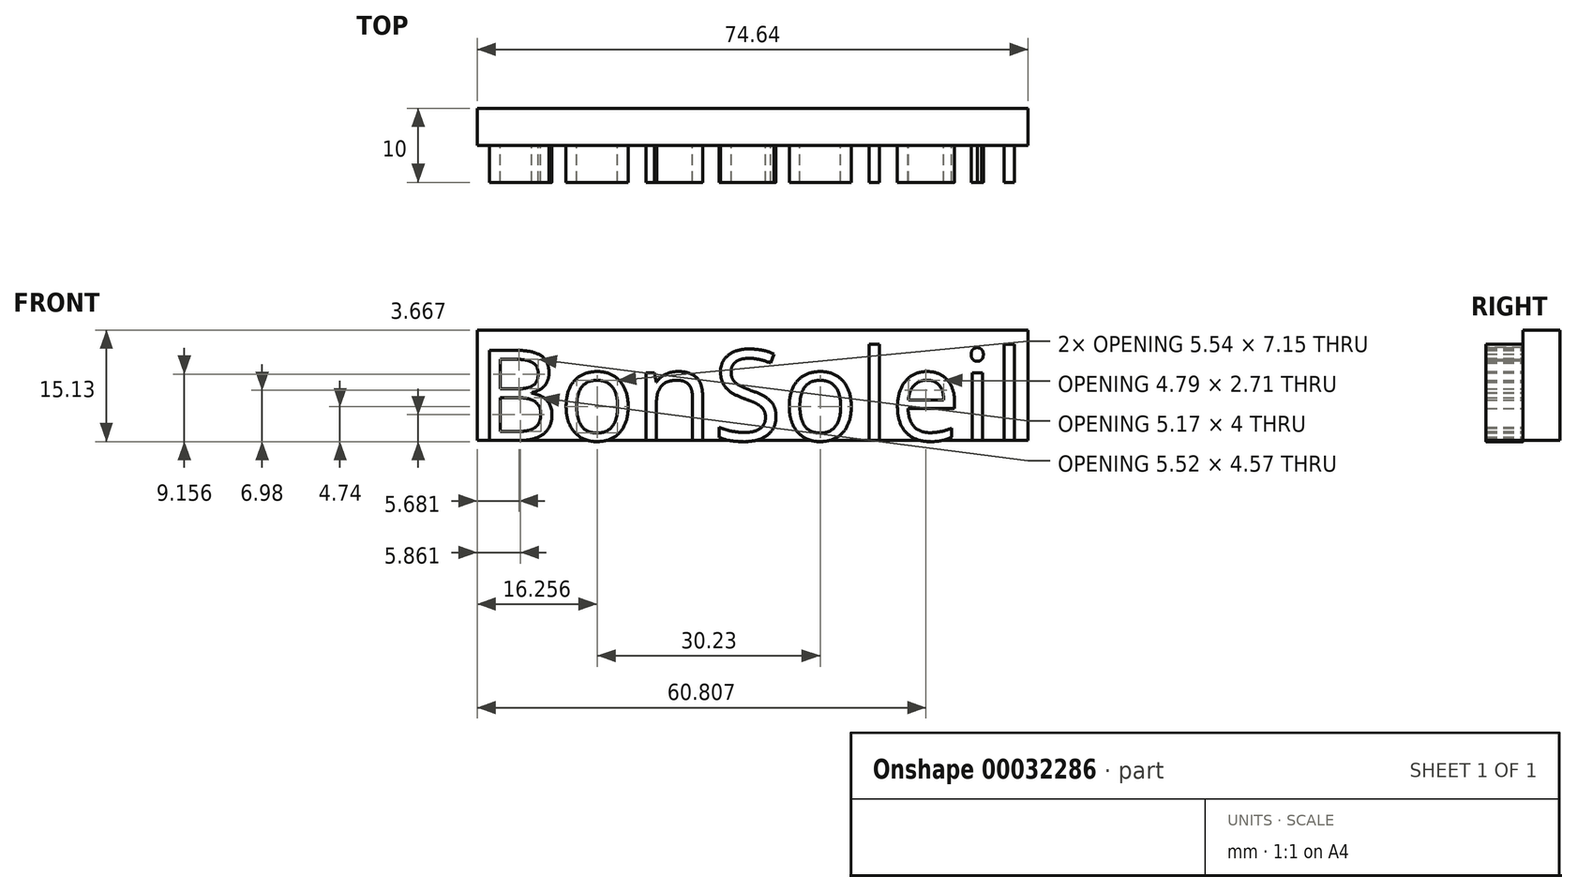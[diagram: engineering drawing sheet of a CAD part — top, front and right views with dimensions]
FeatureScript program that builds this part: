
annotation { "Feature Type Name" : "Feature", "Feature Type Description" : "" }
export const myFeature = defineFeature(function(context is Context, id is Id, definition is map)
    precondition{}
    {
        {
            var Q0;
            Q0=qCreatedBy(makeId("Front.planeOp"),FACE);
            var sketch = newSketch(context, id + "F0", { "sketchPlane" : qUnion([Q0])});
            skText(sketch, "E0", { "text": "BonSoleil\n", "fontName": "OpenSans-Regular.ttf"});
            const initialGuessF0  = {"E0": [0, 0, 1, 0, 0.01232]};
            skSetInitialGuess(sketch, initialGuessF0);
            skSolve(sketch);
        }
        {
            var Q0;
            Q0=makeQuery(id+"F0.imprint","IMPRINT",FACE,{"disambiguationData":[TD([[makeQuery(id+"F0.imprint","IMPRINT",EDGE,{"derivedFrom":sQuery(id+"F0.wireOp",EDGE,"E0.sketch_text.stroke-42")}),-1.0]])]});
            var Q1;
            Q1=makeQuery(id+"F0.imprint","IMPRINT",FACE,{"disambiguationData":[TD([[makeQuery(id+"F0.imprint","IMPRINT",EDGE,{"derivedFrom":sQuery(id+"F0.wireOp",EDGE,"E0.sketch_text.stroke-59")}),-1.0]])]});
            var Q2;
            Q2=makeQuery(id+"F0.imprint","IMPRINT",FACE,{"disambiguationData":[TD([[makeQuery(id+"F0.imprint","IMPRINT",EDGE,{"derivedFrom":sQuery(id+"F0.wireOp",EDGE,"E0.sketch_text.stroke-101")}),-1.0]])]});
            var Q3;
            Q3=makeQuery(id+"F0.imprint","IMPRINT",FACE,{"disambiguationData":[TD([[makeQuery(id+"F0.imprint","IMPRINT",EDGE,{"derivedFrom":sQuery(id+"F0.wireOp",EDGE,"E0.sketch_text.stroke-124")}),-1.0]])]});
            var Q4;
            Q4=makeQuery(id+"F0.imprint","IMPRINT",FACE,{"disambiguationData":[TD([[makeQuery(id+"F0.imprint","IMPRINT",EDGE,{"derivedFrom":sQuery(id+"F0.wireOp",EDGE,"E0.sketch_text.stroke-128")}),-1.0]])]});
            var Q5;
            Q5=makeQuery(id+"F0.imprint","IMPRINT",FACE,{"disambiguationData":[TD([[makeQuery(id+"F0.imprint","IMPRINT",EDGE,{"derivedFrom":sQuery(id+"F0.wireOp",EDGE,"E0.sketch_text.stroke-136")}),-1.0]])]});
            var Q6;
            Q6=makeQuery(id+"F0.imprint","IMPRINT",FACE,{"disambiguationData":[TD([[makeQuery(id+"F0.imprint","IMPRINT",EDGE,{"derivedFrom":sQuery(id+"F0.wireOp",EDGE,"E0.sketch_text.stroke-25")}),-1.0]])]});
            var Q7;
            Q7=makeQuery(id+"F0.imprint","IMPRINT",FACE,{"disambiguationData":[TD([[makeQuery(id+"F0.imprint","IMPRINT",EDGE,{"derivedFrom":sQuery(id+"F0.wireOp",EDGE,"E0.sketch_text.stroke-84")}),-1.0]])]});
            var Q8;
            Q8=makeQuery(id+"F0.imprint","IMPRINT",FACE,{"disambiguationData":[TD([[makeQuery(id+"F0.imprint","IMPRINT",EDGE,{"derivedFrom":sQuery(id+"F0.wireOp",EDGE,"E0.sketch_text.stroke-105")}),-1.0]])]});
            var Q9;
            Q9=makeQuery(id+"F0.imprint","IMPRINT",FACE,{"disambiguationData":[TD([[makeQuery(id+"F0.imprint","IMPRINT",EDGE,{"derivedFrom":sQuery(id+"F0.wireOp",EDGE,"E0.sketch_text.stroke-0")}),-1.0]])]});
            extrude(context, id + "F1", {"entities" : qUnion([Q0, Q1, Q2, Q3, Q4, Q5, Q6, Q7, Q8, Q9]), "depth" : 5 * mm});
        }
        {
            var Q0;
            Q0=qCreatedBy(makeId("Front.planeOp"),FACE);
            var sketch = newSketch(context, id + "F2", { "sketchPlane" : qUnion([Q0])});
            skLineSegment(sketch, "E1.bottom", {"start": v(0, 0) * mm, "end": v(74.64, 0) * mm});
            skLineSegment(sketch, "E1.top", {"start": v(0, 14.96) * mm, "end": v(74.64, 14.96) * mm});
            skLineSegment(sketch, "E1.left", {"start": v(0, 0) * mm, "end": v(0, 14.96) * mm});
            skLineSegment(sketch, "E1.right", {"start": v(74.64, 0) * mm, "end": v(74.64, 14.96) * mm});
            skSolve(sketch);
        }
        {
            var Q0;
            Q0=makeQuery(id+"F2.imprint","IMPRINT",FACE,{"disambiguationData":[TD([[makeQuery(id+"F2.imprint","IMPRINT",EDGE,{"derivedFrom":sQuery(id+"F2.wireOp",EDGE,"E1.bottom")}),1.0]])]});
            extrude(context, id + "F3", {"entities" : qUnion([Q0]), "oppositeDirection" : true, "depth" : 5 * mm});
        }
    });
